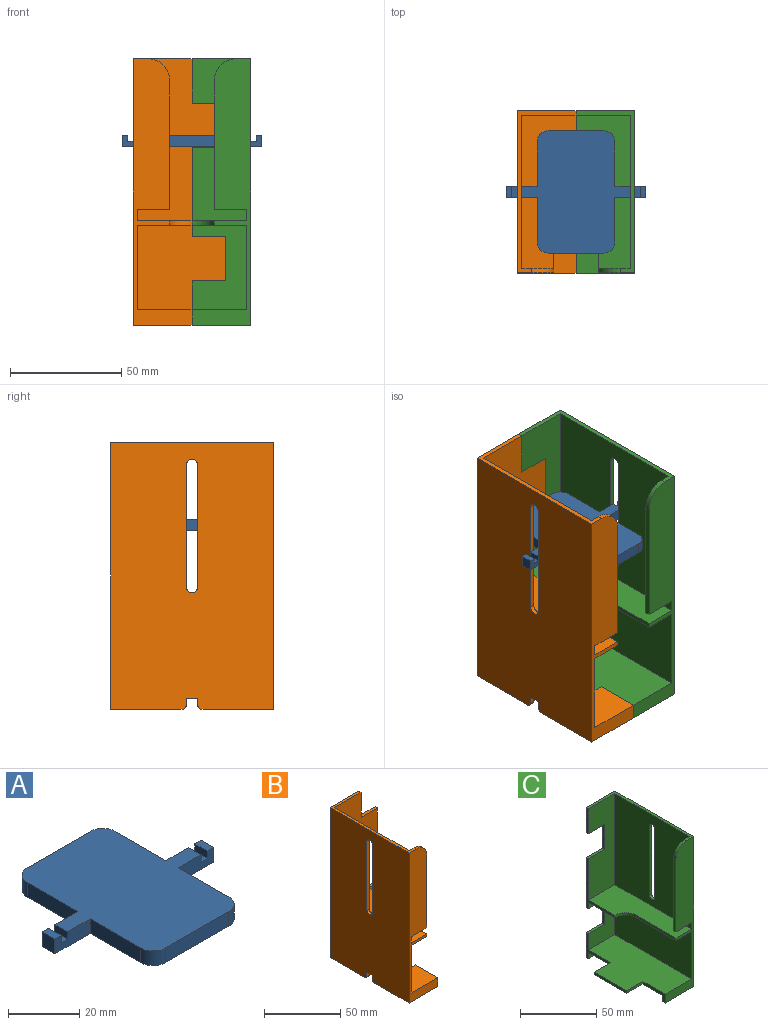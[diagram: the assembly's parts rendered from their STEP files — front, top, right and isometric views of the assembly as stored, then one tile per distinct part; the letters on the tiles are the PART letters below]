
ASSEMBLY  parts=3 mates=3
PART A: 26 faces, bbox 63x55x5 mm
  f0: plane 5x2.5mm, normal (0,0,1), area 12.5mm2, adj f8,f9,f10,f25
  f1: plane 55x53mm, normal (0,0,1), area 1993.5mm2, adj f2,f3,f4,f5,f6,f7,f8,f10
  f2: plane 14x5mm, normal (0,-1,0), area 63.8mm2, adj f1,f3,f17,f18,f19,f20,f21,f22
  f3: plane 20x5mm, normal (-1,0,0), area 100mm2, adj f1,f2,f4,f19
  f4: cylinder r=5mm len=5mm, axis (0,0,-1), area 39.3mm2, adj f1,f3,f5,f19
  f5: plane 25x5mm, normal (0,-1,0), area 125mm2, adj f1,f4,f6,f19
  f6: cylinder r=5mm len=5mm, axis (0,0,-1), area 39.3mm2, adj f1,f5,f7,f19
  f7: plane 20x5mm, normal (1,0,0), area 100mm2, adj f1,f6,f8,f19
  f8: plane 14x5mm, normal (0,-1,0), area 63.8mm2, adj f0,f1,f7,f9,f19,f23,f24,f25
  f9: plane 5x5mm, normal (1,0,0), area 25mm2, adj f0,f8,f10,f19
  f10: plane 14x5mm, normal (0,1,0), area 63.8mm2, adj f0,f1,f9,f11,f19,f23,f24,f25
  f11: plane 20x5mm, normal (1,0,0), area 100mm2, adj f1,f10,f12,f19
  f12: cylinder r=5mm len=5mm, axis (0,0,-1), area 39.3mm2, adj f1,f11,f13,f19
  f13: plane 25x5mm, normal (0,1,0), area 125mm2, adj f1,f12,f14,f19
  f14: cylinder r=5mm len=5mm, axis (0,0,-1), area 39.3mm2, adj f1,f13,f15,f19
  f15: plane 20x5mm, normal (-1,0,0), area 100mm2, adj f1,f14,f16,f19
  f16: plane 14x5mm, normal (0,1,0), area 63.8mm2, adj f1,f15,f17,f18,f19,f20,f21,f22
  f17: plane 5x5mm, normal (-1,0,0), area 25mm2, adj f2,f16,f18,f19
  f18: plane 5x2.5mm, normal (0,0,1), area 12.5mm2, adj f2,f16,f17,f21
  f19: plane 63x55mm, normal (0,0,-1), area 2043.5mm2, adj f2,f3,f4,f5,f6,f7,f8,f9
  f20: plane 5x2.5mm, normal (0,0,1), area 12.5mm2, adj f2,f16,f21,f22
  f21: plane 5x2.5mm, normal (1,0,0), area 12.5mm2, adj f2,f16,f18,f20
  f22: plane 5x2.5mm, normal (-1,0,0), area 12.5mm2, adj f1,f2,f16,f20
  f23: plane 5x2.5mm, normal (0,0,1), area 12.5mm2, adj f8,f10,f24,f25
  f24: plane 5x2.5mm, normal (1,0,0), area 12.5mm2, adj f1,f8,f10,f23
  f25: plane 5x2.5mm, normal (-1,0,0), area 12.5mm2, adj f0,f8,f10,f23
PART B: 45 faces, bbox 41.5x73x120 mm
  f0: plane 20.5x7mm, normal (1,0,0), area 51mm2, adj f22,f32,f33,f34,f35,f44
  f1: plane 22.5x20mm, normal (1,0,0), area 81mm2, adj f22,f23,f24,f25,f26,f35,f40,f42
  f2: plane 40x26.5mm, normal (1,0,0), area 129mm2, adj f23,f26,f27,f28,f29,f31,f37,f39
  f3: plane 20x2mm, normal (1,0,0), area 40mm2, adj f26,f29,f30,f36
  f4: cylinder r=2.5mm len=5mm, axis (1,0,0), area 15.7mm2, adj f5,f7,f14,f19
  f5: plane 55x2mm, normal (0,1,0), area 110mm2, adj f4,f6,f14,f19
  f6: cylinder r=2.5mm len=5mm, axis (1,0,0), area 15.7mm2, adj f5,f7,f14,f19
  f7: plane 55x2mm, normal (0,-1,0), area 110mm2, adj f4,f6,f14,f19
  f8: plane 3x2mm, normal (0,-1,0), area 6mm2, adj f19,f20,f21,f35
  f9: plane 3x2mm, normal (0,1,0), area 6mm2, adj f17,f18,f19,f35
  f10: plane 58x2mm, normal (1,0,0), area 116mm2, adj f11,f12,f13,f34
  f11: plane 14.5x2mm, normal (0,0,-1), area 29mm2, adj f10,f12,f14,f34
  f12: plane 68x14.5mm, normal (0,1,0), area 964.5mm2, adj f10,f11,f13,f14,f30
  f13: cylinder r=10mm len=10mm, axis (0,-1,0), area 31.4mm2, adj f10,f12,f30,f34
  f14: plane 73x71mm, normal (1,0,0), area 4752.4mm2, adj f4,f5,f6,f7,f11,f12,f28,f29
  f15: plane 36.5x2mm, normal (1,0,0), area 73mm2, adj f27,f28,f31,f34
  f16: plane 71x38mm, normal (1,0,0), area 2698mm2, adj f22,f23,f31,f34
  f17: plane 32x5mm, normal (1,0,0), area 159.1mm2, adj f9,f18,f32,f33,f35
  f18: cylinder r=2mm len=2mm, axis (-1,0,0), area 6.3mm2, adj f9,f17,f19,f32
  f19: plane 120x73mm, normal (-1,0,0), area 8438.6mm2, adj f4,f5,f6,f7,f8,f9,f18,f20
  f20: cylinder r=2mm len=2mm, axis (1,0,0), area 6.3mm2, adj f8,f19,f21,f24
  f21: plane 32x5mm, normal (1,0,0), area 159.1mm2, adj f8,f20,f24,f25,f35
  f22: plane 71x24.5mm, normal (0,0,1), area 1289.5mm2, adj f0,f1,f16,f23,f34,f42,f43,f44
  f23: plane 39.5x38mm, normal (0,-1,0), area 1231mm2, adj f1,f2,f16,f22,f31,f39,f40,f41
  f24: plane 32x26.5mm, normal (0,0,-1), area 113mm2, adj f1,f19,f20,f21,f25,f26
  f25: plane 24.5x5mm, normal (0,-1,0), area 122.5mm2, adj f1,f21,f24,f35
  f26: plane 120x41.5mm, normal (0,1,0), area 3780mm2, adj f1,f2,f3,f19,f24,f30,f36,f37
  f27: cylinder r=10mm len=10mm, axis (0,0,-1), area 31.4mm2, adj f2,f15,f28,f31
  f28: plane 71x24.5mm, normal (0,0,1), area 1296mm2, adj f2,f14,f15,f27,f29,f34
  f29: plane 73x39.5mm, normal (0,-1,0), area 2088.5mm2, adj f2,f3,f14,f28,f30,f36,f37,f38
  f30: plane 73x26.5mm, normal (0,0,1), area 204mm2, adj f3,f12,f13,f14,f19,f26,f29,f34
  f31: plane 71x24.5mm, normal (0,0,-1), area 1296mm2, adj f2,f15,f16,f23,f27,f34
  f32: plane 32x26.5mm, normal (0,0,-1), area 113mm2, adj f0,f17,f18,f19,f33,f34
  f33: plane 24.5x5mm, normal (0,1,0), area 122.5mm2, adj f0,f17,f32,f35
  f34: plane 120x26.5mm, normal (0,-1,0), area 1405mm2, adj f0,f10,f11,f13,f14,f15,f16,f19
  f35: plane 69x26.5mm, normal (0,0,-1), area 1250.5mm2, adj f0,f1,f8,f9,f17,f19,f21,f25
  f36: plane 15x2mm, normal (0,0,1), area 30mm2, adj f3,f26,f29,f38
  f37: plane 15x2mm, normal (0,0,-1), area 30mm2, adj f2,f26,f29,f38
  f38: plane 20x2mm, normal (1,0,0), area 40mm2, adj f26,f29,f36,f37
  f39: plane 15x2mm, normal (0,0,1), area 30mm2, adj f2,f23,f26,f41
  f40: plane 15x2mm, normal (0,0,-1), area 30mm2, adj f1,f23,f26,f41
  f41: plane 20x2mm, normal (1,0,0), area 40mm2, adj f23,f26,f39,f40
  f42: plane 15x2mm, normal (0,-1,0), area 30mm2, adj f1,f22,f35,f43
  f43: plane 30x2mm, normal (1,0,0), area 60mm2, adj f22,f35,f42,f44
  f44: plane 15x2mm, normal (0,1,0), area 30mm2, adj f0,f22,f35,f43
PART C: 45 faces, bbox 41.5x73x120 mm
  f0: plane 20.5x7mm, normal (-1,0,0), area 51mm2, adj f5,f8,f24,f26,f28,f44
  f1: plane 22.5x20mm, normal (-1,0,0), area 81mm2, adj f3,f5,f23,f24,f31,f32,f37,f42
  f2: plane 40x26.5mm, normal (-1,0,0), area 129mm2, adj f3,f4,f12,f14,f16,f23,f36,f40
  f3: plane 120x26.5mm, normal (0,1,0), area 2580mm2, adj f1,f2,f10,f13,f32,f35,f36,f37
  f4: plane 73x24.5mm, normal (0,-1,0), area 1488.5mm2, adj f2,f11,f13,f14,f35,f39,f40,f41
  f5: plane 69x41.5mm, normal (0,0,-1), area 2150.5mm2, adj f0,f1,f10,f25,f26,f27,f29,f30
  f6: plane 71x38mm, normal (-1,0,0), area 2698mm2, adj f8,f12,f23,f24
  f7: plane 68x14.5mm, normal (0,1,0), area 964.5mm2, adj f9,f11,f13,f17,f22
  f8: plane 120x26.5mm, normal (0,-1,0), area 1405mm2, adj f0,f6,f9,f10,f11,f12,f13,f14
  f9: plane 58x2mm, normal (-1,0,0), area 116mm2, adj f7,f8,f17,f22
  f10: plane 120x73mm, normal (1,0,0), area 8438.6mm2, adj f3,f5,f8,f13,f18,f19,f20,f21
  f11: plane 73x71mm, normal (-1,0,0), area 4752.4mm2, adj f4,f7,f8,f13,f14,f18,f19,f20
  f12: plane 71x24.5mm, normal (0,0,-1), area 1296mm2, adj f2,f6,f8,f15,f16,f23
  f13: plane 73x26.5mm, normal (0,0,1), area 204mm2, adj f3,f4,f7,f8,f10,f11,f17,f35
  f14: plane 71x24.5mm, normal (0,0,1), area 1296mm2, adj f2,f4,f8,f11,f15,f16
  f15: plane 36.5x2mm, normal (-1,0,0), area 73mm2, adj f8,f12,f14,f16
  f16: cylinder r=10mm len=10mm, axis (0,0,-1), area 31.4mm2, adj f2,f12,f14,f15
  f17: cylinder r=10mm len=10mm, axis (0,1,0), area 31.4mm2, adj f7,f8,f9,f13
  f18: plane 55x2mm, normal (0,-1,0), area 110mm2, adj f10,f11,f19,f21
  f19: cylinder r=2.5mm len=5mm, axis (1,0,0), area 15.7mm2, adj f10,f11,f18,f20
  f20: plane 55x2mm, normal (0,1,0), area 110mm2, adj f10,f11,f19,f21
  f21: cylinder r=2.5mm len=5mm, axis (1,0,0), area 15.7mm2, adj f10,f11,f18,f20
  f22: plane 14.5x2mm, normal (0,0,-1), area 29mm2, adj f7,f8,f9,f11
  f23: plane 38x24.5mm, normal (0,-1,0), area 631mm2, adj f1,f2,f6,f12,f24,f36,f37,f38
  f24: plane 71x39.5mm, normal (0,0,1), area 2189.5mm2, adj f0,f1,f6,f8,f23,f42,f43,f44
  f25: plane 3x2mm, normal (0,1,0), area 6mm2, adj f5,f10,f27,f34
  f26: plane 24.5x5mm, normal (0,1,0), area 122.5mm2, adj f0,f5,f27,f28
  f27: plane 32x5mm, normal (-1,0,0), area 159.1mm2, adj f5,f25,f26,f28,f34
  f28: plane 32x26.5mm, normal (0,0,-1), area 113mm2, adj f0,f8,f10,f26,f27,f34
  f29: plane 3x2mm, normal (0,-1,0), area 6mm2, adj f5,f10,f30,f33
  f30: plane 32x5mm, normal (-1,0,0), area 159.1mm2, adj f5,f29,f31,f32,f33
  f31: plane 24.5x5mm, normal (0,-1,0), area 122.5mm2, adj f1,f5,f30,f32
  f32: plane 32x26.5mm, normal (0,0,-1), area 113mm2, adj f1,f3,f10,f30,f31,f33
  f33: cylinder r=2mm len=2mm, axis (1,0,0), area 6.3mm2, adj f10,f29,f30,f32
  f34: cylinder r=2mm len=2mm, axis (-1,0,0), area 6.3mm2, adj f10,f25,f27,f28
  f35: plane 20x2mm, normal (-1,0,0), area 40mm2, adj f3,f4,f13,f39
  f36: plane 15x2mm, normal (0,0,-1), area 30mm2, adj f2,f3,f23,f38
  f37: plane 15x2mm, normal (0,0,1), area 30mm2, adj f1,f3,f23,f38
  f38: plane 20x2mm, normal (-1,0,0), area 40mm2, adj f3,f23,f36,f37
  f39: plane 15x2mm, normal (0,0,-1), area 30mm2, adj f3,f4,f35,f41
  f40: plane 15x2mm, normal (0,0,1), area 30mm2, adj f2,f3,f4,f41
  f41: plane 20x2mm, normal (-1,0,0), area 40mm2, adj f3,f4,f39,f40
  f42: plane 15x2mm, normal (0,1,0), area 30mm2, adj f1,f5,f24,f43
  f43: plane 30x2mm, normal (-1,0,0), area 60mm2, adj f5,f24,f42,f44
  f44: plane 15x2mm, normal (0,-1,0), area 30mm2, adj f0,f5,f24,f43
PLACE A t=(-28.69,-4.65,40.05)mm
PLACE B t=(-28.69,-4.65,4.76)mm
PLACE C t=(-28.69,-4.65,4.76)mm fixed
MATE fastened C.f3 <-> B.f26  axis (0,1,0) through (-13.69,31.85,49.76)mm
MATE planar C.f10 <-> A.f24  axis (1,0,0) through (-2.19,-4.65,19.16)mm
MATE planar A.f8 <-> C.f20  axis (0,-1,0) through (-4.51,-7.15,42.43)mm
